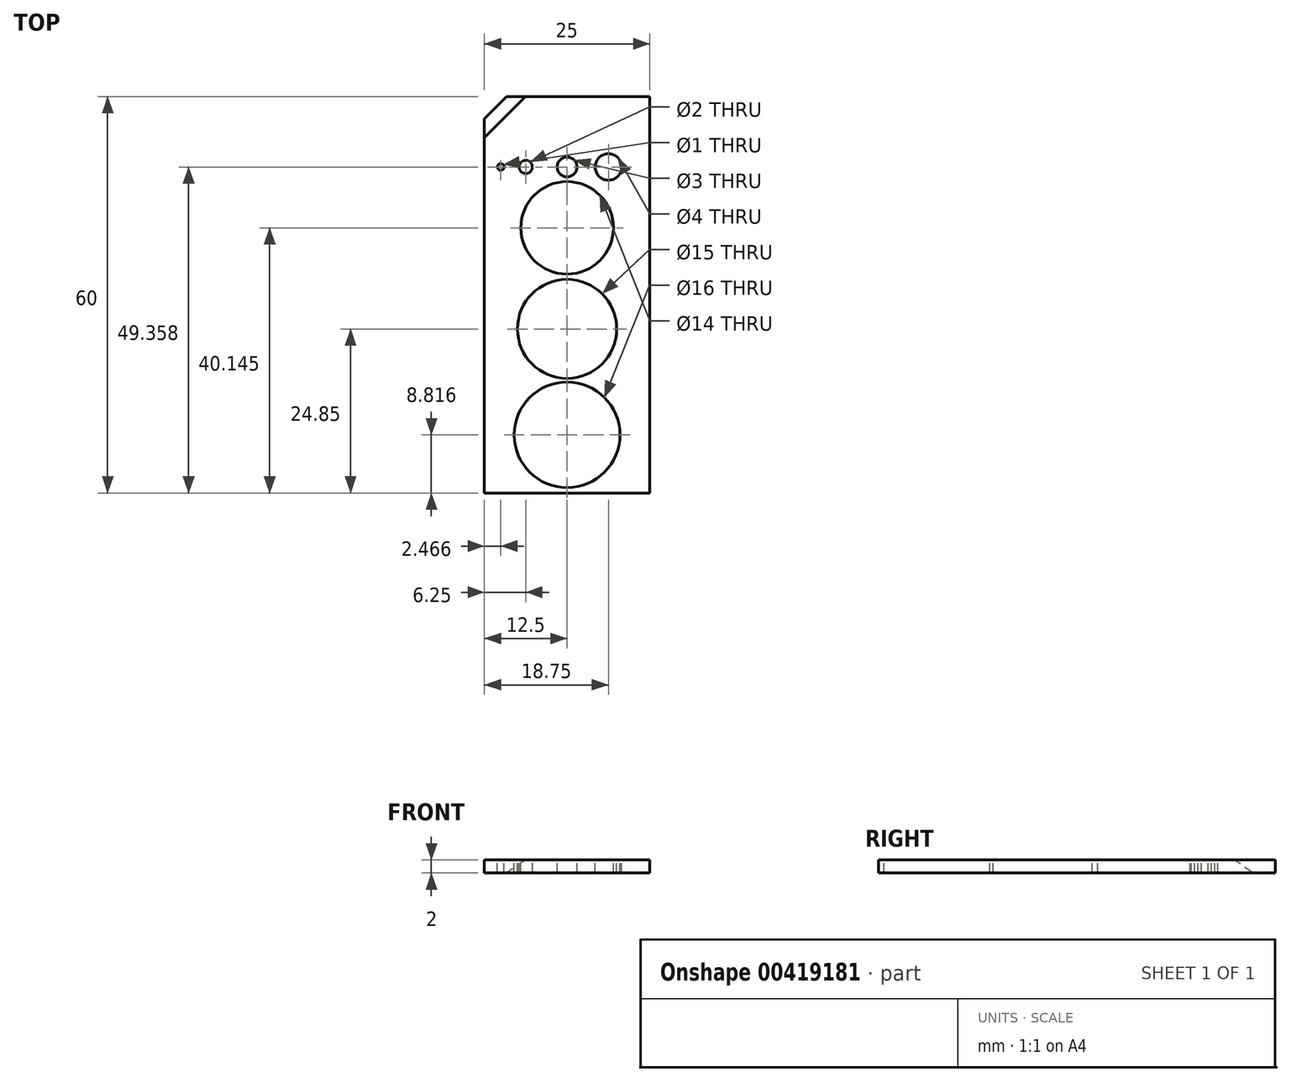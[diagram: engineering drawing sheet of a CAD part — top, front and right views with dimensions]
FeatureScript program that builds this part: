
annotation { "Feature Type Name" : "Feature", "Feature Type Description" : "" }
export const myFeature = defineFeature(function(context is Context, id is Id, definition is map)
    precondition{}
    {
        {
            var Q0;
            Q0=qCreatedBy(makeId("Top.planeOp"),FACE);
            var sketch = newSketch(context, id + "F0", { "sketchPlane" : qUnion([Q0])});
            skLineSegment(sketch, "E0.top", {"start": v(12.5, -30) * mm, "end": v(-12.5, -30) * mm});
            skLineSegment(sketch, "E0.left", {"start": v(12.5, 30) * mm, "end": v(12.5, -30) * mm});
            skPoint(sketch, "E0.middle", {"position": v(0, 0) * mm});
            skLineSegment(sketch, "E1", {"start": v(-12.5, 26.63) * mm, "end": v(-9.13, 30) * mm});
            skLineSegment(sketch, "E2", {"start": v(-12.5, -30) * mm, "end": v(-12.5, 26.63) * mm});
            skLineSegment(sketch, "E3", {"start": v(-9.13, 30) * mm, "end": v(12.5, 30) * mm});
            skSolve(sketch);
        }
        {
            var Q0;
            Q0=makeQuery(id+"F0.imprint","IMPRINT",FACE,{"disambiguationData":[TD([[makeQuery(id+"F0.imprint","IMPRINT",EDGE,{"derivedFrom":sQuery(id+"F0.wireOp",EDGE,"E0.top")}),-1.0]])]});
            extrude(context, id + "F1", {"entities" : qUnion([Q0]), "depth" : 2 * mm});
        }
        {
            var Q0;
            Q0=makeQuery(id+"F1.opExtrude","CAP_EDGE",EDGE,{"disambiguationData":[OSD([sQuery(id+"F0.wireOp",EDGE,"E1")])],"isStart":false});
            chamfer(context, id + "F2", {"entities" : qUnion([Q0]), "width" : 2 * mm, "tangentPropagation" : true});
        }
        {
            var Q0;
            Q0=makeQuery(id+"F1.opExtrude","CAP_FACE",FACE,{"disambiguationData":[OSD([sQuery(id+"F0.wireOp",EDGE,"E0.top"),sQuery(id+"F0.wireOp",EDGE,"E0.left"),sQuery(id+"F0.wireOp",EDGE,"E1"),sQuery(id+"F0.wireOp",EDGE,"E2"),sQuery(id+"F0.wireOp",EDGE,"E3")])],"isStart":false});
            var sketch = newSketch(context, id + "F3", { "sketchPlane" : qUnion([Q0])});
            skLineSegment(sketch, "E4", {"start": v(0, 30) * mm, "end": v(0, -30) * mm, "construction": true});
            skLineSegment(sketch, "E5", {"start": v(-12.5, 19.36) * mm, "end": v(12.5, 19.36) * mm, "construction": true});
            skLineSegment(sketch, "E6", {"start": v(0, 19.36) * mm, "end": v(-12.5, 19.36) * mm, "construction": true});
            skLineSegment(sketch, "E7", {"start": v(12.5, 19.36) * mm, "end": v(0, 19.36) * mm, "construction": true});
            skLineSegment(sketch, "E8", {"start": v(6.25, 19.36) * mm, "end": v(6.25, 30) * mm, "construction": true});
            skLineSegment(sketch, "E9", {"start": v(-6.25, 19.36) * mm, "end": v(-6.3, 30) * mm, "construction": true});
            skCircle(sketch, "E10", {"center": v(-6.25, 19.36) * mm, "radius": 1 * mm});
            skCircle(sketch, "E11", {"center": v(0, 19.36) * mm, "radius": 1.5 * mm});
            skCircle(sketch, "E12", {"center": v(6.25, 19.36) * mm, "radius": 2 * mm});
            skCircle(sketch, "E13", {"center": v(-10.03, 19.36) * mm, "radius": 0.5 * mm});
            skSolve(sketch);
        }
        {
            var Q0;
            Q0=makeQuery(id+"F3.imprint","IMPRINT",FACE,{"disambiguationData":[TD([[makeQuery(id+"F3.imprint","IMPRINT",EDGE,{"derivedFrom":sQuery(id+"F3.wireOp",EDGE,"E10")}),1.0]])]});
            var Q1;
            Q1=makeQuery(id+"F3.imprint","IMPRINT",FACE,{"disambiguationData":[TD([[makeQuery(id+"F3.imprint","IMPRINT",EDGE,{"derivedFrom":sQuery(id+"F3.wireOp",EDGE,"E13")}),1.0]])]});
            var Q2;
            Q2=makeQuery(id+"F3.imprint","IMPRINT",FACE,{"disambiguationData":[TD([[makeQuery(id+"F3.imprint","IMPRINT",EDGE,{"derivedFrom":sQuery(id+"F3.wireOp",EDGE,"E11")}),1.0]])]});
            var Q3;
            Q3=makeQuery(id+"F3.imprint","IMPRINT",FACE,{"disambiguationData":[TD([[makeQuery(id+"F3.imprint","IMPRINT",EDGE,{"derivedFrom":sQuery(id+"F3.wireOp",EDGE,"E12")}),1.0]])]});
            extrude(context, id + "F4", {"entities" : qUnion([Q0, Q1, Q2, Q3]), "operationType" : NewBodyOperationType.REMOVE, "oppositeDirection" : true, "depth" : 25.4 * mm});
        }
        {
            var Q0;
            Q0=makeQuery(id+"F1.opExtrude","CAP_FACE",FACE,{"disambiguationData":[OSD([sQuery(id+"F0.wireOp",EDGE,"E0.top"),sQuery(id+"F0.wireOp",EDGE,"E0.left"),sQuery(id+"F0.wireOp",EDGE,"E1"),sQuery(id+"F0.wireOp",EDGE,"E2"),sQuery(id+"F0.wireOp",EDGE,"E3")])],"isStart":false});
            var sketch = newSketch(context, id + "F5", { "sketchPlane" : qUnion([Q0])});
            skCircle(sketch, "E14", {"center": v(0, 10.14) * mm, "radius": 7 * mm});
            skCircle(sketch, "E15", {"center": v(0, -5.15) * mm, "radius": 7.5 * mm});
            skCircle(sketch, "E16", {"center": v(0, -21.18) * mm, "radius": 8 * mm});
            skSolve(sketch);
        }
        {
            var Q0;
            Q0=makeQuery(id+"F5.imprint","IMPRINT",FACE,{"disambiguationData":[TD([[makeQuery(id+"F5.imprint","IMPRINT",EDGE,{"derivedFrom":sQuery(id+"F5.wireOp",EDGE,"E15")}),1.0]])]});
            var Q1;
            Q1=makeQuery(id+"F5.imprint","IMPRINT",FACE,{"disambiguationData":[TD([[makeQuery(id+"F5.imprint","IMPRINT",EDGE,{"derivedFrom":sQuery(id+"F5.wireOp",EDGE,"E16")}),1.0]])]});
            var Q2;
            Q2=makeQuery(id+"F5.imprint","IMPRINT",FACE,{"disambiguationData":[TD([[makeQuery(id+"F5.imprint","IMPRINT",EDGE,{"derivedFrom":sQuery(id+"F5.wireOp",EDGE,"E14")}),1.0]])]});
            extrude(context, id + "F6", {"entities" : qUnion([Q0, Q1, Q2]), "operationType" : NewBodyOperationType.REMOVE, "oppositeDirection" : true, "depth" : 25.4 * mm});
        }
    });
